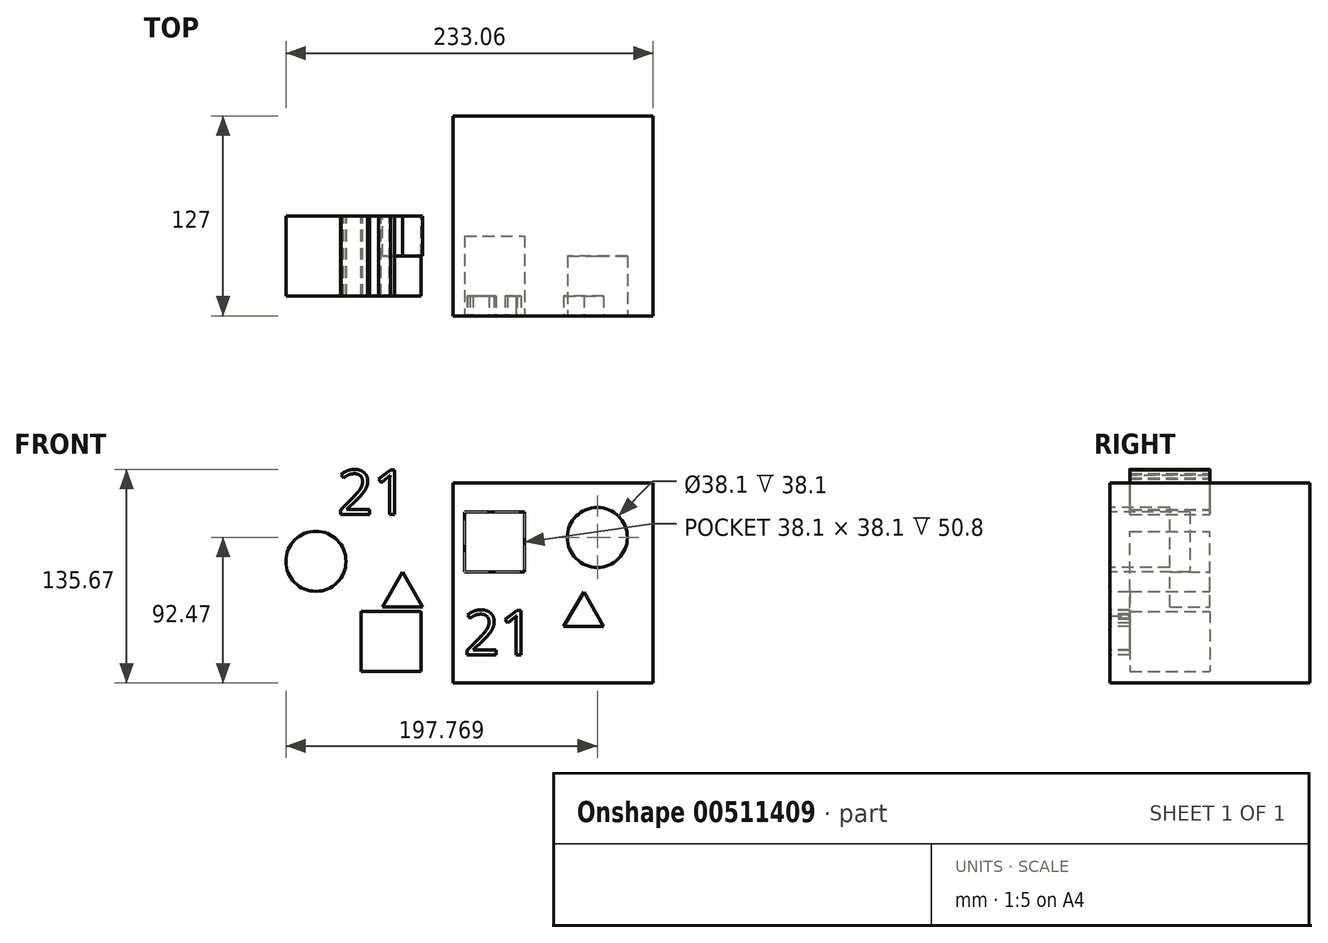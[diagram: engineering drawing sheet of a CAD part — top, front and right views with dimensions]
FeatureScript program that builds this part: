
annotation { "Feature Type Name" : "Feature", "Feature Type Description" : "" }
export const myFeature = defineFeature(function(context is Context, id is Id, definition is map)
    precondition{}
    {
        {
            var Q0;
            Q0=qCreatedBy(makeId("Front.planeOp"),FACE);
            var sketch = newSketch(context, id + "F0", { "sketchPlane" : qUnion([Q0])});
            skLineSegment(sketch, "E0.bottom", {"start": v(-51.52, 65.87) * mm, "end": v(75.48, 65.87) * mm});
            skLineSegment(sketch, "E0.top", {"start": v(-51.52, -61.13) * mm, "end": v(75.48, -61.13) * mm});
            skLineSegment(sketch, "E0.left", {"start": v(-51.52, 65.87) * mm, "end": v(-51.52, -61.13) * mm});
            skLineSegment(sketch, "E0.right", {"start": v(75.48, 65.87) * mm, "end": v(75.48, -61.13) * mm});
            skSolve(sketch);
        }
        {
            var Q0;
            Q0 = qSketchRegion(id + "F0", true);
            extrude(context, id + "F1", {"entities" : qUnion([Q0]), "depth" : 127 * mm, "symmetric" : true});
        }
        {
            var Q0;
            Q0=makeQuery(id+"F1.opExtrude","CAP_FACE",FACE,{"disambiguationData":[OSD([sQuery(id+"F0.wireOp",EDGE,"E0.bottom"),sQuery(id+"F0.wireOp",EDGE,"E0.top"),sQuery(id+"F0.wireOp",EDGE,"E0.left"),sQuery(id+"F0.wireOp",EDGE,"E0.right")])],"isStart":false});
            var sketch = newSketch(context, id + "F2", { "sketchPlane" : qUnion([Q0])});
            skLineSegment(sketch, "E1.bottom", {"start": v(-44.1, 47.5) * mm, "end": v(-6, 47.5) * mm});
            skLineSegment(sketch, "E1.top", {"start": v(-44.1, 9.4) * mm, "end": v(-6, 9.4) * mm});
            skLineSegment(sketch, "E1.left", {"start": v(-44.1, 47.5) * mm, "end": v(-44.1, 9.4) * mm});
            skLineSegment(sketch, "E1.right", {"start": v(-6, 47.5) * mm, "end": v(-6, 9.4) * mm});
            skSolve(sketch);
        }
        {
            var Q0;
            Q0=makeQuery(id+"F2.imprint","IMPRINT",FACE,{"disambiguationData":[TD([[makeQuery(id+"F2.imprint","IMPRINT",EDGE,{"derivedFrom":sQuery(id+"F2.wireOp",EDGE,"E1.bottom")}),-1.0]])]});
            extrude(context, id + "F3", {"entities" : qUnion([Q0]), "operationType" : NewBodyOperationType.REMOVE, "oppositeDirection" : true, "depth" : 50.8 * mm});
        }
        {
            var Q0;
            Q0=makeQuery(id+"F1.opExtrude","CAP_FACE",FACE,{"disambiguationData":[OSD([sQuery(id+"F0.wireOp",EDGE,"E0.bottom"),sQuery(id+"F0.wireOp",EDGE,"E0.top"),sQuery(id+"F0.wireOp",EDGE,"E0.left"),sQuery(id+"F0.wireOp",EDGE,"E0.right")])],"isStart":false});
            var sketch = newSketch(context, id + "F4", { "sketchPlane" : qUnion([Q0])});
            skCircle(sketch, "E2", {"center": v(40.19, 31.34) * mm, "radius": 19.05 * mm});
            skSolve(sketch);
        }
        {
            var Q0;
            Q0=makeQuery(id+"F4.imprint","IMPRINT",FACE,{"disambiguationData":[TD([[makeQuery(id+"F4.imprint","IMPRINT",EDGE,{"derivedFrom":sQuery(id+"F4.wireOp",EDGE,"E2")}),1.0]])]});
            extrude(context, id + "F5", {"entities" : qUnion([Q0]), "operationType" : NewBodyOperationType.REMOVE, "oppositeDirection" : true, "depth" : 38.1 * mm});
        }
        {
            var Q0;
            Q0=makeQuery(id+"F1.opExtrude","CAP_FACE",FACE,{"disambiguationData":[OSD([sQuery(id+"F0.wireOp",EDGE,"E0.bottom"),sQuery(id+"F0.wireOp",EDGE,"E0.top"),sQuery(id+"F0.wireOp",EDGE,"E0.left"),sQuery(id+"F0.wireOp",EDGE,"E0.right")])],"isStart":false});
            var sketch = newSketch(context, id + "F6", { "sketchPlane" : qUnion([Q0])});
            skText(sketch, "E3", { "text": "21", "fontName": "OpenSans-Regular.ttf"});
            const initialGuessF6  = {"E3": [-0.04458, -0.04323, 1, 0, 0.02838]};
            skSetInitialGuess(sketch, initialGuessF6);
            skSolve(sketch);
        }
        {
            var Q0;
            Q0 = qSketchRegion(id + "F6", true);
            extrude(context, id + "F7", {"entities" : qUnion([Q0]), "operationType" : NewBodyOperationType.REMOVE, "oppositeDirection" : true, "depth" : 25.4 * mm, "symmetric" : true});
        }
        {
            var Q0;
            Q0=makeQuery(id+"F1.opExtrude","CAP_FACE",FACE,{"disambiguationData":[OSD([sQuery(id+"F0.wireOp",EDGE,"E0.bottom"),sQuery(id+"F0.wireOp",EDGE,"E0.top"),sQuery(id+"F0.wireOp",EDGE,"E0.left"),sQuery(id+"F0.wireOp",EDGE,"E0.right")])],"isStart":false});
            var sketch = newSketch(context, id + "F8", { "sketchPlane" : qUnion([Q0])});
            skCircle(sketch, "E4.cCircle", {"center": v(33.41, -25.23) * mm, "radius": 14.66 * mm, "construction": true});
            skLineSegment(sketch, "E4.0", {"start": v(44.15, -25.35) * mm, "end": v(18.75, -25.07) * mm});
            skLineSegment(sketch, "E4.1", {"start": v(18.75, -25.07) * mm, "end": v(31.7, -3.21) * mm});
            skLineSegment(sketch, "E4.2", {"start": v(31.7, -3.21) * mm, "end": v(44.15, -25.35) * mm});
            skSolve(sketch);
        }
        {
            var Q0;
            Q0=makeQuery(id+"F8.imprint","IMPRINT",FACE,{"disambiguationData":[TD([[makeQuery(id+"F8.imprint","IMPRINT",EDGE,{"derivedFrom":sQuery(id+"F8.wireOp",EDGE,"E4.0")}),-1.0]])]});
            extrude(context, id + "F9", {"entities" : qUnion([Q0]), "operationType" : NewBodyOperationType.REMOVE, "oppositeDirection" : true, "depth" : 25.4 * mm, "offsetDistance" : 25.4 * mm, "symmetric" : true});
        }
        {
            var Q0;
            Q0=qCreatedBy(makeId("Front.planeOp"),FACE);
            var sketch = newSketch(context, id + "F10", { "sketchPlane" : qUnion([Q0])});
            skCircle(sketch, "E5", {"center": v(-138.53, 16.12) * mm, "radius": 19.05 * mm});
            skSolve(sketch);
        }
        {
            var Q0;
            Q0 = qSketchRegion(id + "F10", true);
            extrude(context, id + "F11", {"entities" : qUnion([Q0]), "depth" : 50.8 * mm, "offsetDistance" : 25.4 * mm});
        }
        {
            var Q0;
            Q0=qCreatedBy(makeId("Front.planeOp"),FACE);
            var sketch = newSketch(context, id + "F12", { "sketchPlane" : qUnion([Q0])});
            skLineSegment(sketch, "E6.bottom", {"start": v(-109.91, -15.64) * mm, "end": v(-71.81, -15.64) * mm});
            skLineSegment(sketch, "E6.top", {"start": v(-109.91, -53.74) * mm, "end": v(-71.81, -53.74) * mm});
            skLineSegment(sketch, "E6.left", {"start": v(-109.91, -15.64) * mm, "end": v(-109.91, -53.74) * mm});
            skLineSegment(sketch, "E6.right", {"start": v(-71.81, -15.64) * mm, "end": v(-71.81, -53.74) * mm});
            skSolve(sketch);
        }
        {
            var Q0;
            Q0=makeQuery(id+"F12.imprint","IMPRINT",FACE,{"disambiguationData":[TD([[makeQuery(id+"F12.imprint","IMPRINT",EDGE,{"derivedFrom":sQuery(id+"F12.wireOp",EDGE,"E6.bottom")}),-1.0]])]});
            extrude(context, id + "F13", {"entities" : qUnion([Q0]), "depth" : 50.8 * mm});
        }
        {
            var Q0;
            Q0=qCreatedBy(makeId("Front.planeOp"),FACE);
            var sketch = newSketch(context, id + "F14", { "sketchPlane" : qUnion([Q0])});
            skText(sketch, "E7", { "text": "21", "fontName": "OpenSans-Regular.ttf"});
            const initialGuessF14  = {"E7": [-0.1249, 0.046, 1, 0, 0.02838]};
            skSetInitialGuess(sketch, initialGuessF14);
            skSolve(sketch);
        }
        {
            var Q0;
            Q0 = qSketchRegion(id + "F14", true);
            extrude(context, id + "F15", {"entities" : qUnion([Q0]), "depth" : 50.8 * mm, "offsetDistance" : 25.4 * mm});
        }
        {
            var Q0;
            Q0=qCreatedBy(makeId("Front.planeOp"),FACE);
            var sketch = newSketch(context, id + "F16", { "sketchPlane" : qUnion([Q0])});
            skCircle(sketch, "E8.cCircle", {"center": v(-88.9, -0.04) * mm, "radius": 7.33 * mm, "construction": true});
            skLineSegment(sketch, "E8.0", {"start": v(-96.24, -12.74) * mm, "end": v(-83.54, 9.26) * mm});
            skLineSegment(sketch, "E8.1", {"start": v(-83.54, 9.26) * mm, "end": v(-70.84, -12.74) * mm});
            skLineSegment(sketch, "E8.2", {"start": v(-70.84, -12.74) * mm, "end": v(-96.24, -12.74) * mm});
            skPoint(sketch, "E8.0.midPoint", {"position": v(-96.24, -0.04) * mm});
            skSolve(sketch);
        }
        {
            var Q0;
            Q0=makeQuery(id+"F16.imprint","IMPRINT",FACE,{"disambiguationData":[TD([[makeQuery(id+"F16.imprint","IMPRINT",EDGE,{"derivedFrom":sQuery(id+"F16.wireOp",EDGE,"E8.0")}),-1.0]])]});
            extrude(context, id + "F17", {"entities" : qUnion([Q0]), "operationType" : NewBodyOperationType.ADD, "depth" : 25.4 * mm, "offsetDistance" : 25.4 * mm});
        }
    });
